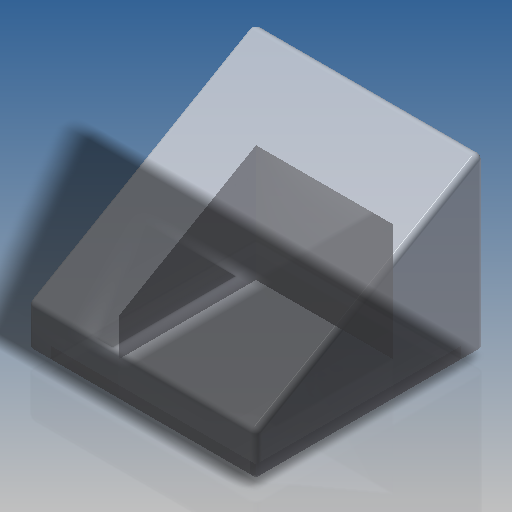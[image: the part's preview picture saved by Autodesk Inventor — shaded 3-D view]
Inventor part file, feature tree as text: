
AUTODESK INVENTOR PART (.ipt)
format: ipt  version: 2018.3 (Build 223284000, 284)  size: 227,840 bytes
history: native  units: in
note: dims shown in document units (in); Inventor stores cm internally (conversion verified against a paired STEP export)
features: extrude x4, sketch x2, fillet x1, other x1
ambient origin geometry x8: Origin, YZ Plane, XZ Plane, XY Plane, X Axis, Y Axis, Z Axis, Center Point
bodies: Solid2 (feature_tree)
feature tree (8):
  sketch  "Sketch10"  dims[d7=0.0591in d22=0.0079in d91=0.315in]
  extrude  "Extrusion6"  Depth=0.315in
  sketch  "Sketch11"  dims[d92=0.252in d94=0.315in d95=0.0in d96=0.189in d97=0.063in d98=0.0in d99=0.0in d100=0.0in d101=0.0in d102=0.0in d103=30.0deg d104=0.0157in d105=0.0157in d106=0.0157in d107=0.0in d108=0.0in d109=0.052in d110=0.063in d111=0.063in d112=0.189in d113=0.0in]
  extrude  "Extrusion9"  Depth=0.315in TaperAngle=0.0deg
  extrude  "Extrusion7"  Depth=0.189in
  extrude  "Extrusion8"  Depth=0.063in TaperAngle=0.0deg
  fillet  "Fillet1"  [1 undecoded]
  other  "Work Axis1"
note: 1 required parameter value undecoded (feature->parameter linkage not recoverable at this tier; creation-order binding heuristic only, values carry confidence <= 0.55)
